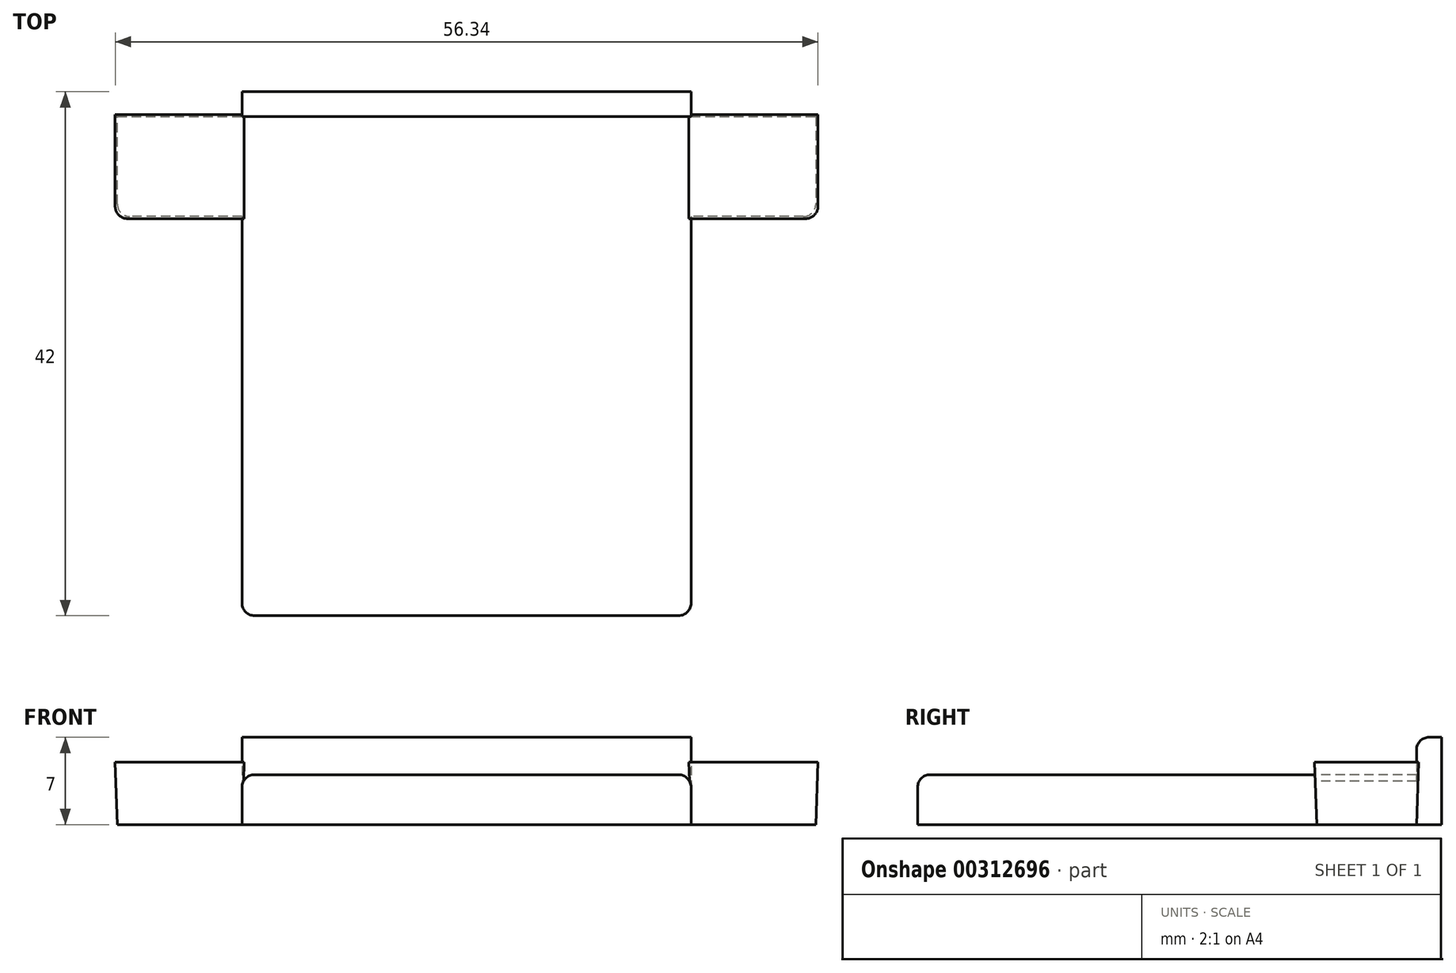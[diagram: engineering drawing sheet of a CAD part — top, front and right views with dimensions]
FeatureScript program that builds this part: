
annotation { "Feature Type Name" : "Feature", "Feature Type Description" : "" }
export const myFeature = defineFeature(function(context is Context, id is Id, definition is map)
    precondition{}
    {
        {
            var Q0;
            Q0=qCreatedBy(makeId("Top.planeOp"),FACE);
            var sketch = newSketch(context, id + "F0", { "sketchPlane" : qUnion([Q0])});
            skLineSegment(sketch, "E0.top", {"start": v(0, -40) * mm, "end": v(36, -40) * mm});
            skLineSegment(sketch, "E0.left", {"start": v(0, 0) * mm, "end": v(0, -8) * mm});
            skLineSegment(sketch, "E0.right", {"start": v(36, 0) * mm, "end": v(36, -8) * mm});
            skLineSegment(sketch, "E1.bottom", {"start": v(36, 0) * mm, "end": v(46, 0) * mm});
            skLineSegment(sketch, "E1.top", {"start": v(36, -8) * mm, "end": v(46, -8) * mm});
            skLineSegment(sketch, "E1.right", {"start": v(46, 0) * mm, "end": v(46, -8) * mm});
            skLineSegment(sketch, "E2", {"start": v(18, 0) * mm, "end": v(18, -40) * mm, "construction": true});
            skLineSegment(sketch, "E3.MirrorCS", {"start": v(0, -8) * mm, "end": v(-10, -8) * mm});
            skLineSegment(sketch, "E4.MirrorCS", {"start": v(-10, 0) * mm, "end": v(-10, -8) * mm});
            skLineSegment(sketch, "E5.MirrorCS", {"start": v(0, 0) * mm, "end": v(-10, 0) * mm});
            skLineSegment(sketch, "E6.bottom", {"start": v(0, 0) * mm, "end": v(36, 0) * mm});
            skLineSegment(sketch, "E6.top", {"start": v(0, 2) * mm, "end": v(36, 2) * mm});
            skLineSegment(sketch, "E6.left", {"start": v(0, 0) * mm, "end": v(0, 2) * mm});
            skLineSegment(sketch, "E6.right", {"start": v(36, 0) * mm, "end": v(36, 2) * mm});
            skLineSegment(sketch, "E7", {"start": v(0, -8) * mm, "end": v(0, -40) * mm});
            skLineSegment(sketch, "E8", {"start": v(36, -8) * mm, "end": v(36, -40) * mm});
            skSolve(sketch);
        }
        {
            var Q0;
            Q0=makeQuery(id+"F0.imprint","IMPRINT",FACE,{"disambiguationData":[TD([[makeQuery(id+"F0.imprint","IMPRINT",EDGE,{"derivedFrom":sQuery(id+"F0.wireOp",EDGE,"E6.bottom")}),1.0]])]});
            extrude(context, id + "F1", {"entities" : qUnion([Q0]), "depth" : 7 * mm});
        }
        {
            var Q0;
            {var subQ1=sQuery(id+"F0.wireOp",EDGE,"E0.top");Q0=makeQuery(id+"F0.imprint","IMPRINT",FACE,{"disambiguationData":[TD([[makeQuery(id+"F0.imprint","IMPRINT",EDGE,{"derivedFrom":subQ1}),1.0]])]});}
            extrude(context, id + "F2", {"entities" : qUnion([Q0]), "operationType" : NewBodyOperationType.ADD, "depth" : 4 * mm});
        }
        {
            var Q0;
            Q0=makeQuery(id+"F0.imprint","IMPRINT",FACE,{"disambiguationData":[TD([[makeQuery(id+"F0.imprint","IMPRINT",EDGE,{"derivedFrom":sQuery(id+"F0.wireOp",EDGE,"E0.left")}),-1.0]])]});
            var Q1;
            Q1=makeQuery(id+"F0.imprint","IMPRINT",FACE,{"disambiguationData":[TD([[makeQuery(id+"F0.imprint","IMPRINT",EDGE,{"derivedFrom":sQuery(id+"F0.wireOp",EDGE,"E1.bottom")}),-1.0]])]});
            extrude(context, id + "F3", {"entities" : qUnion([Q0, Q1]), "operationType" : NewBodyOperationType.ADD, "depth" : 5 * mm, "hasDraft" : true, "draftAngle" : 2 * degree});
        }
        {
            var Q0;
            Q0=makeQuery(id+"F1.opExtrude","CAP_EDGE",EDGE,{"disambiguationData":[OSD([sQuery(id+"F0.wireOp",EDGE,"E6.bottom")])],"isStart":false});
            var Q1;
            Q1=makeQuery(id+"F3.opExtrude","SWEPT_EDGE",EDGE,{"disambiguationData":[OSD([sQuery(id+"F0.wireOp",EDGE,"E3.MirrorCS"),sQuery(id+"F0.wireOp",EDGE,"E4.MirrorCS")])]});
            var Q2;
            Q2=makeQuery(id+"F3.opExtrude","SWEPT_EDGE",EDGE,{"disambiguationData":[OSD([sQuery(id+"F0.wireOp",EDGE,"E1.top"),sQuery(id+"F0.wireOp",EDGE,"E1.right")])]});
            var Q3;
            Q3=makeQuery(id+"F2.opExtrude","SWEPT_EDGE",EDGE,{"disambiguationData":[OSD([sQuery(id+"F0.wireOp",EDGE,"E0.top"),sQuery(id+"F0.wireOp",EDGE,"E8")])]});
            var Q4;
            Q4=makeQuery(id+"F2.opExtrude","SWEPT_EDGE",EDGE,{"disambiguationData":[OSD([sQuery(id+"F0.wireOp",EDGE,"E0.top"),sQuery(id+"F0.wireOp",EDGE,"E7")])]});
            var Q5;
            Q5=makeQuery(id+"F2.opExtrude","CAP_EDGE",EDGE,{"disambiguationData":[OSD([sQuery(id+"F0.wireOp",EDGE,"E0.top")])],"isStart":false});
            var Q6;
            Q6=makeQuery(id+"F2.opExtrude","CAP_EDGE",EDGE,{"disambiguationData":[OSD([sQuery(id+"F0.wireOp",EDGE,"E0.right"),sQuery(id+"F0.wireOp",EDGE,"E8")])],"isStart":false});
            var Q7;
            Q7=makeQuery(id+"F2.opExtrude","CAP_EDGE",EDGE,{"disambiguationData":[OSD([sQuery(id+"F0.wireOp",EDGE,"E0.left"),sQuery(id+"F0.wireOp",EDGE,"E7")])],"isStart":false});
            fillet(context, id + "F4", {"entities" : qUnion([Q0, Q1, Q2, Q3, Q4, Q5, Q6, Q7]), "radius" : 1 * mm, "tangentPropagation" : true, "allowEdgeOverflow" : false});
        }
    });
